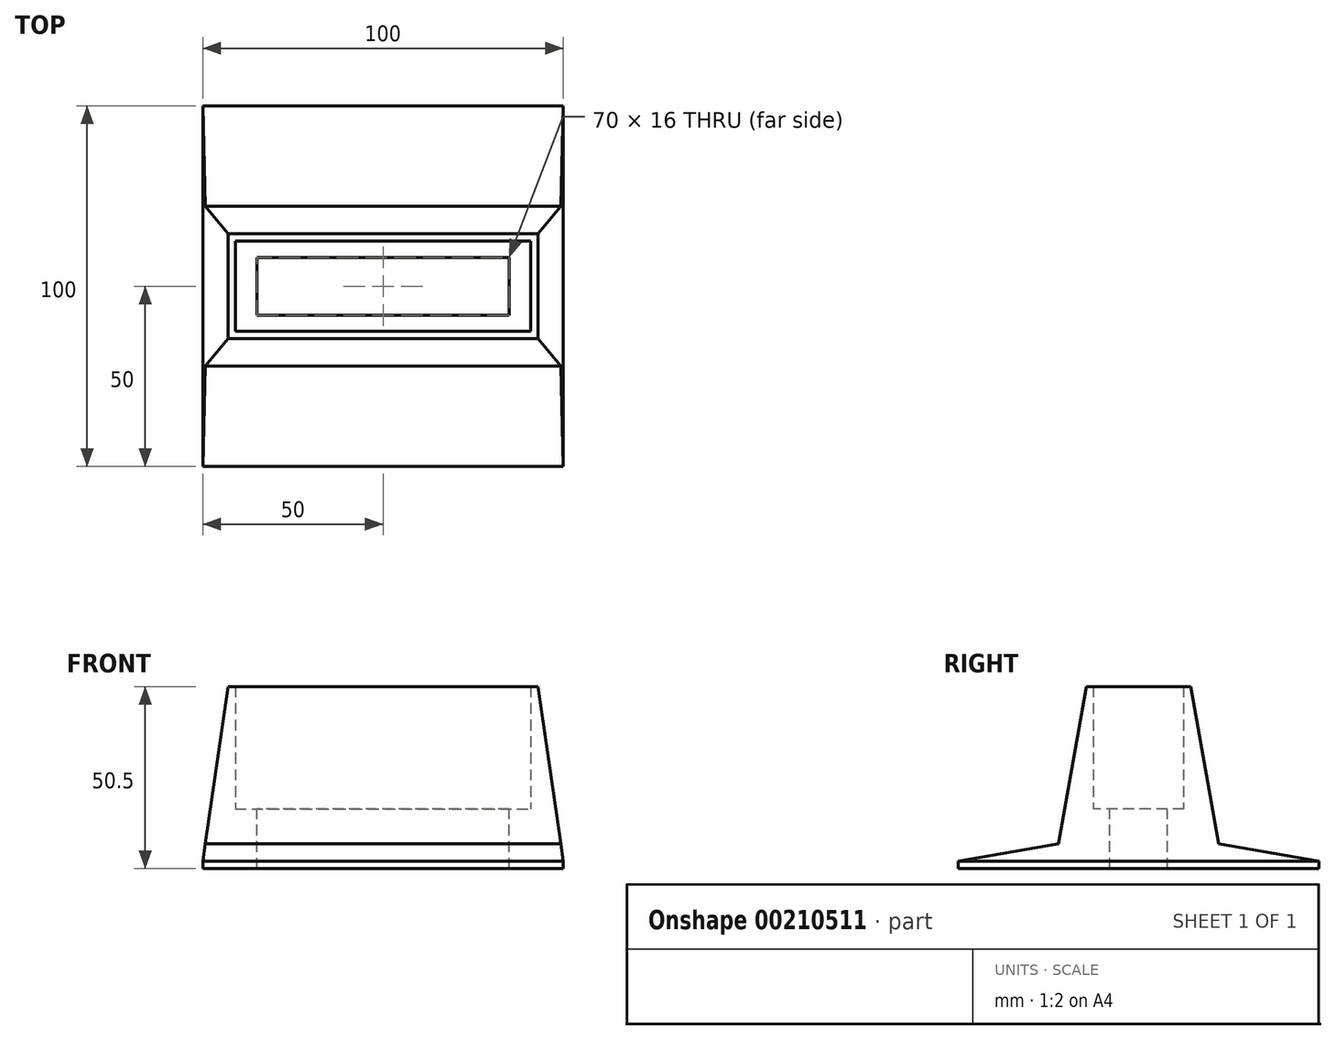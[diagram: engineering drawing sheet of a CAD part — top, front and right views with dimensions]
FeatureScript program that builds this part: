
annotation { "Feature Type Name" : "Feature", "Feature Type Description" : "" }
export const myFeature = defineFeature(function(context is Context, id is Id, definition is map)
    precondition{}
    {
        {
            var Q0;
            Q0=qCreatedBy(makeId("Top.planeOp"),FACE);
            var sketch = newSketch(context, id + "F0", { "sketchPlane" : qUnion([Q0])});
            skLineSegment(sketch, "E0.bottom", {"start": v(-41, 12.5) * mm, "end": v(41, 12.5) * mm});
            skLineSegment(sketch, "E0.top", {"start": v(-41, -12.5) * mm, "end": v(41, -12.5) * mm});
            skLineSegment(sketch, "E0.left", {"start": v(-41, 12.5) * mm, "end": v(-41, -12.5) * mm});
            skLineSegment(sketch, "E0.right", {"start": v(41, 12.5) * mm, "end": v(41, -12.5) * mm});
            skPoint(sketch, "E0.middle", {"position": v(0, 0) * mm});
            skLineSegment(sketch, "E1.bottom", {"start": v(-50, 50) * mm, "end": v(50, 50) * mm});
            skLineSegment(sketch, "E1.top", {"start": v(-50, -50) * mm, "end": v(50, -50) * mm});
            skLineSegment(sketch, "E1.left", {"start": v(-50, 50) * mm, "end": v(-50, -50) * mm});
            skLineSegment(sketch, "E1.right", {"start": v(50, 50) * mm, "end": v(50, -50) * mm});
            skSolve(sketch);
        }
        {
            var Q0;
            Q0=makeQuery(id+"F0.imprint","IMPRINT",FACE,{"disambiguationData":[TD([[makeQuery(id+"F0.imprint","IMPRINT",EDGE,{"derivedFrom":sQuery(id+"F0.wireOp",EDGE,"E0.bottom")}),-1.0]])]});
            var Q1;
            Q1=makeQuery(id+"F0.imprint","IMPRINT",FACE,{"disambiguationData":[TD([[makeQuery(id+"F0.imprint","IMPRINT",EDGE,{"derivedFrom":sQuery(id+"F0.wireOp",EDGE,"E0.bottom")}),1.0]])]});
            extrude(context, id + "F1", {"entities" : qUnion([Q0, Q1]), "oppositeDirection" : true, "depth" : 16.5 * mm});
        }
        {
            var Q0;
            Q0=makeQuery(id+"F0.imprint","IMPRINT",FACE,{"disambiguationData":[TD([[makeQuery(id+"F0.imprint","IMPRINT",EDGE,{"derivedFrom":sQuery(id+"F0.wireOp",EDGE,"E0.bottom")}),1.0]])]});
            extrude(context, id + "F2", {"entities" : qUnion([Q0]), "operationType" : NewBodyOperationType.ADD, "depth" : 34 * mm});
        }
        {
            var Q0;
            {var subQ0=sQuery(id+"F0.wireOp",EDGE,"E1.left");Q0=makeQuery(id+"F2.boolean.opBoolean","MERGE",FACE,{"derivedFrom":[makeQuery(id+"F1.opExtrude","SWEPT_FACE",FACE,{"disambiguationData":[OSD([subQ0])]}),makeQuery(id+"F2.opExtrude","SWEPT_FACE",FACE,{"disambiguationData":[OSD([subQ0])]})]});}
            var sketch = newSketch(context, id + "F3", { "sketchPlane" : qUnion([Q0])});
            skLineSegment(sketch, "E2", {"start": v(14.5, 34) * mm, "end": v(22.19, -9.6) * mm});
            skLineSegment(sketch, "E3", {"start": v(22.19, -9.6) * mm, "end": v(50, -14.5) * mm});
            skLineSegment(sketch, "E4", {"start": v(50, -14.5) * mm, "end": v(50, 34) * mm});
            skLineSegment(sketch, "E5", {"start": v(50, 34) * mm, "end": v(14.5, 34) * mm});
            skLineSegment(sketch, "E6", {"start": v(-14.5, 34) * mm, "end": v(-22.19, -9.6) * mm});
            skLineSegment(sketch, "E7", {"start": v(-22.19, -9.6) * mm, "end": v(-50, -14.5) * mm});
            skLineSegment(sketch, "E8", {"start": v(-50, -14.5) * mm, "end": v(-50, 34) * mm});
            skLineSegment(sketch, "E9", {"start": v(-50, 34) * mm, "end": v(-14.5, 34) * mm});
            skSolve(sketch);
        }
        {
            var Q0;
            Q0=makeQuery(id+"F3.imprint","IMPRINT",FACE,{"disambiguationData":[TD([[makeQuery(id+"F3.imprint","IMPRINT",EDGE,{"derivedFrom":sQuery(id+"F3.wireOp",EDGE,"E2")}),1.0]])]});
            var Q1;
            Q1=makeQuery(id+"F3.imprint","IMPRINT",FACE,{"disambiguationData":[TD([[makeQuery(id+"F3.imprint","IMPRINT",EDGE,{"derivedFrom":sQuery(id+"F3.wireOp",EDGE,"E6")}),-1.0]])]});
            extrude(context, id + "F4", {"entities" : qUnion([Q0, Q1]), "operationType" : NewBodyOperationType.REMOVE, "endBound" : BoundingType.THROUGH_ALL, "oppositeDirection" : true, "depth" : 25 * mm});
        }
        {
            var Q0;
            Q0=qCreatedBy(makeId("Front.planeOp"),FACE);
            var sketch = newSketch(context, id + "F5", { "sketchPlane" : qUnion([Q0])});
            skLineSegment(sketch, "E10.0", {"start": v(50, 34) * mm, "end": v(-50, 34) * mm, "construction": true});
            skLineSegment(sketch, "E11.0", {"start": v(-50, 34) * mm, "end": v(-50, -9.6) * mm, "construction": true});
            skLineSegment(sketch, "E12.0", {"start": v(-50, -9.6) * mm, "end": v(-50, -14.5) * mm, "construction": true});
            skLineSegment(sketch, "E13.0", {"start": v(50, 34) * mm, "end": v(50, -9.6) * mm, "construction": true});
            skLineSegment(sketch, "E14.0", {"start": v(50, -9.6) * mm, "end": v(50, -14.5) * mm, "construction": true});
            skLineSegment(sketch, "E15", {"start": v(-43, 34) * mm, "end": v(-50, -14.5) * mm});
            skLineSegment(sketch, "E16", {"start": v(-50, 34) * mm, "end": v(-50, -14.5) * mm});
            skLineSegment(sketch, "E17", {"start": v(-50, 34) * mm, "end": v(-43, 34) * mm});
            skLineSegment(sketch, "E18", {"start": v(43, 34) * mm, "end": v(50, 34) * mm});
            skLineSegment(sketch, "E19", {"start": v(50, 34) * mm, "end": v(50, -14.5) * mm});
            skLineSegment(sketch, "E20", {"start": v(50, -14.5) * mm, "end": v(43, 34) * mm});
            skSolve(sketch);
        }
        {
            var Q0;
            Q0 = qSketchRegion(id + "F5", true);
            extrude(context, id + "F6", {"entities" : qUnion([Q0]), "operationType" : NewBodyOperationType.REMOVE, "endBound" : BoundingType.THROUGH_ALL, "oppositeDirection" : true, "depth" : 25 * mm, "hasSecondDirection" : true, "secondDirectionBound" : SecondDirectionBoundingType.THROUGH_ALL, "secondDirectionOppositeDirection" : false, "secondDirectionDepth" : 25 * mm});
        }
        {
            var Q0;
            Q0=makeQuery(id+"F1.opExtrude","CAP_FACE",FACE,{"disambiguationData":[OSD([sQuery(id+"F0.wireOp",EDGE,"E1.bottom"),sQuery(id+"F0.wireOp",EDGE,"E1.top"),sQuery(id+"F0.wireOp",EDGE,"E1.left"),sQuery(id+"F0.wireOp",EDGE,"E1.right")])],"isStart":true});
            var sketch = newSketch(context, id + "F7", { "sketchPlane" : qUnion([Q0])});
            skLineSegment(sketch, "E21.bottom", {"start": v(35, 8) * mm, "end": v(-35, 8) * mm});
            skLineSegment(sketch, "E21.top", {"start": v(35, -8) * mm, "end": v(-35, -8) * mm});
            skLineSegment(sketch, "E21.left", {"start": v(35, 8) * mm, "end": v(35, -8) * mm});
            skLineSegment(sketch, "E21.right", {"start": v(-35, 8) * mm, "end": v(-35, -8) * mm});
            skPoint(sketch, "E21.middle", {"position": v(0, 0) * mm});
            skSolve(sketch);
        }
        {
            var Q0;
            Q0 = qSketchRegion(id + "F7", true);
            extrude(context, id + "F8", {"entities" : qUnion([Q0]), "operationType" : NewBodyOperationType.REMOVE, "endBound" : BoundingType.THROUGH_ALL, "oppositeDirection" : true, "depth" : 25 * mm});
        }
    });
